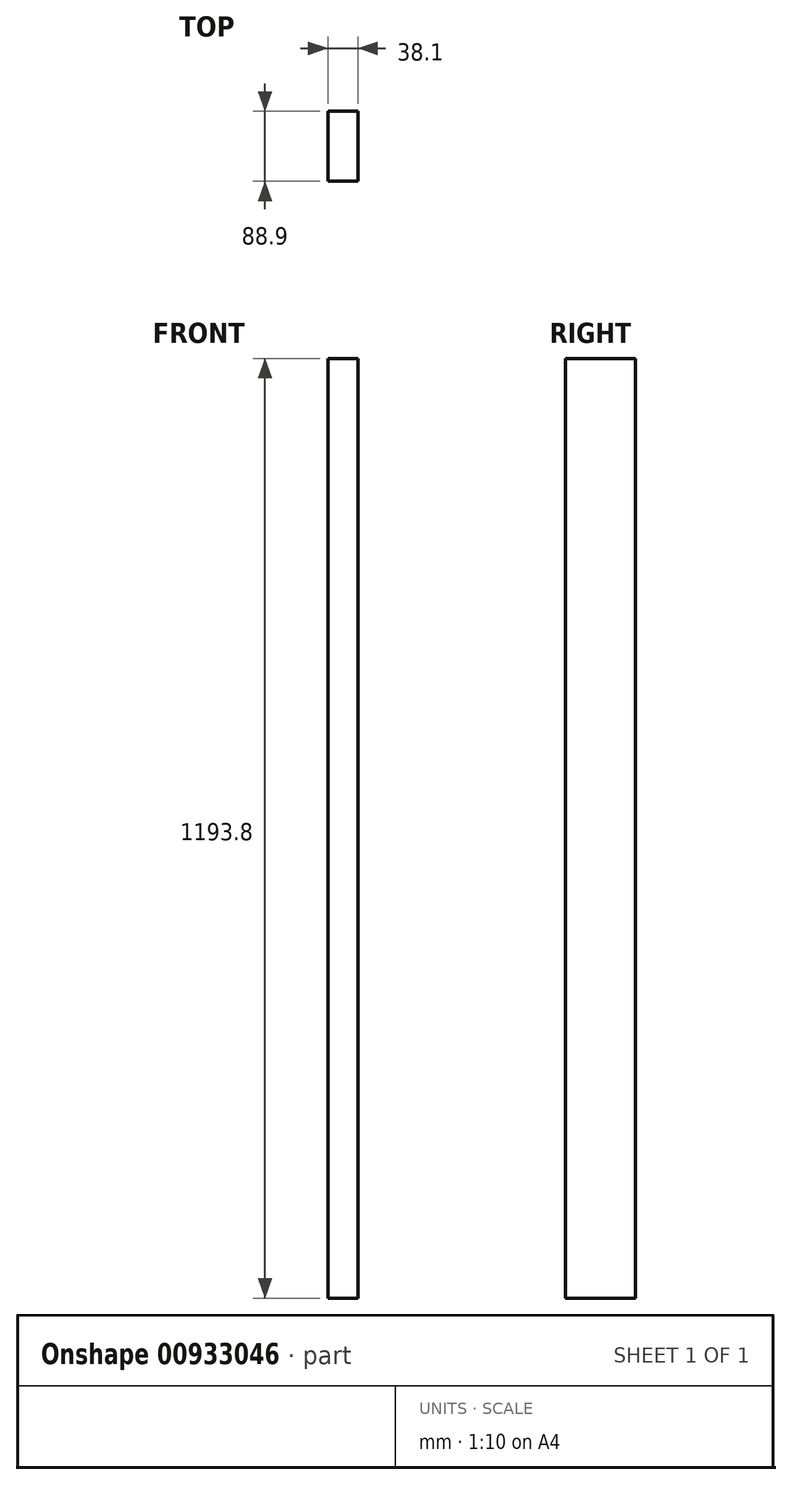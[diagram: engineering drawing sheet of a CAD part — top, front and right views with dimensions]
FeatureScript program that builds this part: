
annotation { "Feature Type Name" : "Feature", "Feature Type Description" : "" }
export const myFeature = defineFeature(function(context is Context, id is Id, definition is map)
    precondition{}
    {
        {
            var Q0;
            Q0=qCreatedBy(makeId("Top.planeOp"),FACE);
            var sketch = newSketch(context, id + "F0", { "sketchPlane" : qUnion([Q0])});
            skLineSegment(sketch, "E0.bottom", {"start": v(19.05, 44.45) * mm, "end": v(-19.05, 44.45) * mm});
            skLineSegment(sketch, "E0.top", {"start": v(19.05, -44.45) * mm, "end": v(-19.05, -44.45) * mm});
            skLineSegment(sketch, "E0.left", {"start": v(19.05, 44.45) * mm, "end": v(19.05, -44.45) * mm});
            skLineSegment(sketch, "E0.right", {"start": v(-19.05, 44.45) * mm, "end": v(-19.05, -44.45) * mm});
            skPoint(sketch, "E0.middle", {"position": v(0, 0) * mm});
            skSolve(sketch);
        }
        {
            var Q0;
            Q0 = qSketchRegion(id + "F0", true);
            extrude(context, id + "F1", {"entities" : qUnion([Q0]), "depth" : 1193.8 * mm, "offsetDistance" : 25.4 * mm});
        }
    });
